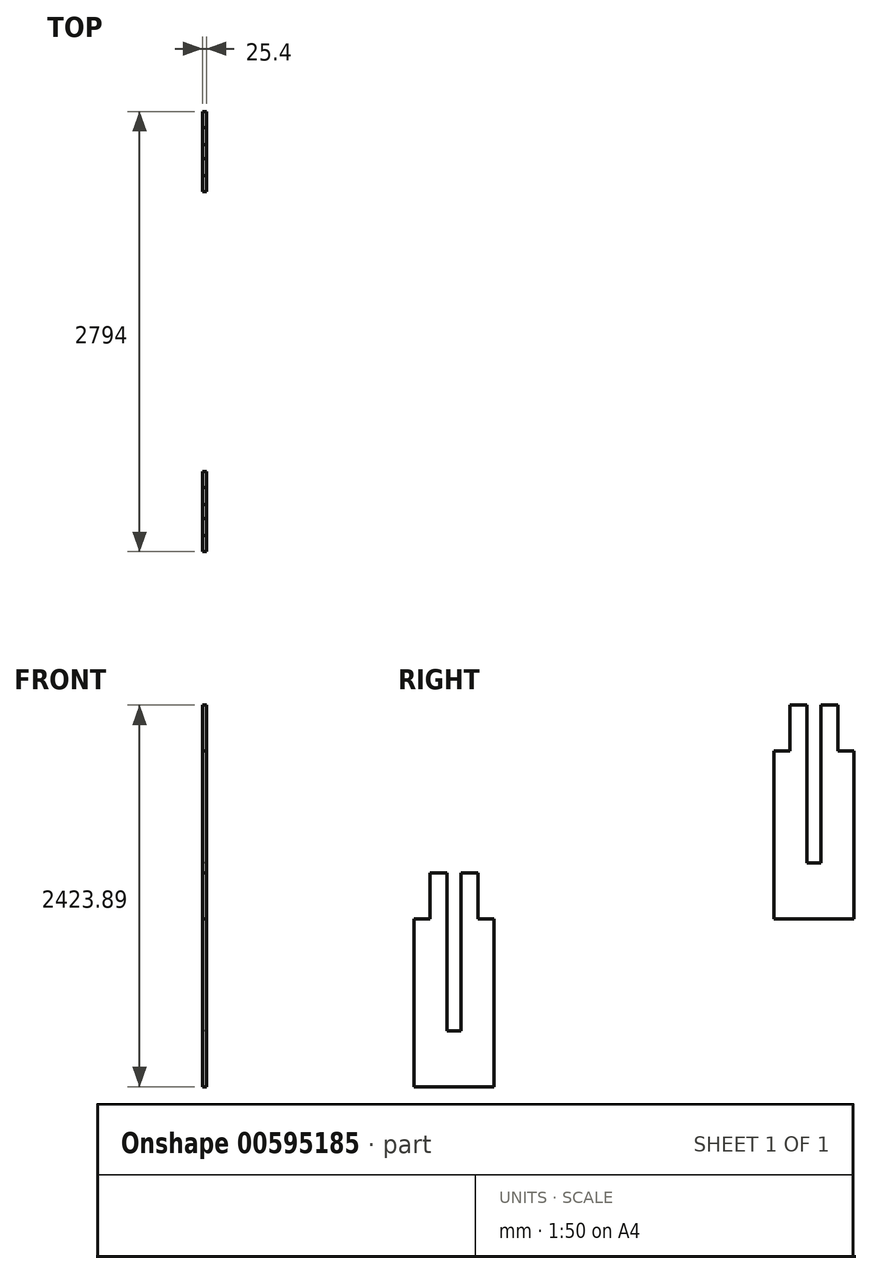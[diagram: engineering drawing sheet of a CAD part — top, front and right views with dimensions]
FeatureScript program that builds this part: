
annotation { "Feature Type Name" : "Feature", "Feature Type Description" : "" }
export const myFeature = defineFeature(function(context is Context, id is Id, definition is map)
    precondition{}
    {
        {
            var Q0;
            Q0=qCreatedBy(makeId("Right.planeOp"),FACE);
            var sketch = newSketch(context, id + "F0", { "sketchPlane" : qUnion([Q0])});
            skLineSegment(sketch, "E0.bottom", {"start": v(1143, -1143) * mm, "end": v(-1143, -1143) * mm});
            skLineSegment(sketch, "E0.right", {"start": v(-1143, -1143) * mm, "end": v(-1143, 1143) * mm});
            skPoint(sketch, "E0.middle", {"position": v(0, 0) * mm});
            skLineSegment(sketch, "E1", {"start": v(0, 0) * mm, "end": v(3173.99, 1480.05) * mm, "construction": true});
            skLineSegment(sketch, "E2", {"start": v(0, 0) * mm, "end": v(-5441.08, -2537.22) * mm, "construction": true});
            skPoint(sketch, "E3.middle", {"position": v(1143, 532.99) * mm});
            skLineSegment(sketch, "E4.bottom", {"start": v(889, 414.55) * mm, "end": v(990.6, 414.55) * mm});
            skLineSegment(sketch, "E4.top", {"start": v(889, -652.25) * mm, "end": v(1397, -652.25) * mm});
            skLineSegment(sketch, "E4.right", {"start": v(1397, 414.55) * mm, "end": v(1397, -652.25) * mm});
            skLineSegment(sketch, "E5", {"start": v(1295.4, 604.05) * mm, "end": v(1295.4, 705.65) * mm});
            skLineSegment(sketch, "E6", {"start": v(1295.4, 705.65) * mm, "end": v(1187.45, 705.65) * mm});
            skLineSegment(sketch, "E7", {"start": v(990.6, 705.65) * mm, "end": v(990.6, 414.55) * mm});
            skLineSegment(sketch, "E8", {"start": v(1295.4, 604.05) * mm, "end": v(1295.4, 414.55) * mm});
            skLineSegment(sketch, "E9", {"start": v(1187.45, 705.65) * mm, "end": v(1187.45, -296.65) * mm});
            skLineSegment(sketch, "E10", {"start": v(1187.45, -296.65) * mm, "end": v(1098.55, -296.65) * mm});
            skLineSegment(sketch, "E11", {"start": v(1098.55, -296.65) * mm, "end": v(1098.55, 705.65) * mm});
            skLineSegment(sketch, "E12.trimOffspring", {"start": v(1098.55, 705.65) * mm, "end": v(990.6, 705.65) * mm});
            skLineSegment(sketch, "E13.trimOffspring", {"start": v(1295.4, 414.55) * mm, "end": v(1397, 414.55) * mm});
            skLineSegment(sketch, "E14.trimOffspring", {"start": v(1143, 1066.39) * mm, "end": v(1143, 1143) * mm});
            skPoint(sketch, "E15.start.orphan", {"position": v(1143, 1066.39) * mm});
            skPoint(sketch, "E16.orphan", {"position": v(1098.55, 1066.39) * mm});
            skPoint(sketch, "E17.end.orphan", {"position": v(1187.45, 1066.39) * mm});
            skLineSegment(sketch, "E18", {"start": v(0, 0) * mm, "end": v(0, 464) * mm, "construction": true});
            skLineSegment(sketch, "E19", {"start": v(889, 414.55) * mm, "end": v(889, -652.25) * mm});
            skLineSegment(sketch, "E20", {"start": v(1143, 532.99) * mm, "end": v(4504.76, 532.99) * mm, "construction": true});
            skLineSegment(sketch, "E21", {"start": v(3173.99, 1480.05) * mm, "end": v(4504.76, 2100.6) * mm, "construction": true});
            skLineSegment(sketch, "E22", {"start": v(-1143, -532.99) * mm, "end": v(-4207, -532.99) * mm, "construction": true});
            skLineSegment(sketch, "E23", {"start": v(-4207, -532.99) * mm, "end": v(-4207, -1440.6) * mm, "construction": true});
            skLineSegment(sketch, "E24", {"start": v(4504.76, 2100.6) * mm, "end": v(6234.34, 2100.6) * mm, "construction": true});
            skLineSegment(sketch, "E25", {"start": v(-4207, -1440.6) * mm, "end": v(-5509.02, -1587.44) * mm, "construction": true});
            skSolve(sketch);
        }
        {
            var Q0;
            Q0 = qSketchRegion(id + "F0", true);
            extrude(context, id + "F1", {"entities" : qUnion([Q0]), "depth" : 25.4 * mm, "offsetDistance" : 25.4 * mm});
        }
        {
            var Q0;
            Q0=makeQuery(id+"F1.opExtrude","SWEPT_BODY",BODY,{"disambiguationData":[OSD([sQuery(id+"F0.wireOp",EDGE,"E4.bottom"),sQuery(id+"F0.wireOp",EDGE,"E4.top"),sQuery(id+"F0.wireOp",EDGE,"E4.right"),sQuery(id+"F0.wireOp",EDGE,"E5"),sQuery(id+"F0.wireOp",EDGE,"E6"),sQuery(id+"F0.wireOp",EDGE,"E7"),sQuery(id+"F0.wireOp",EDGE,"E8"),sQuery(id+"F0.wireOp",EDGE,"E9"),sQuery(id+"F0.wireOp",EDGE,"E10"),sQuery(id+"F0.wireOp",EDGE,"E11"),sQuery(id+"F0.wireOp",EDGE,"E12.trimOffspring"),sQuery(id+"F0.wireOp",EDGE,"E13.trimOffspring"),sQuery(id+"F0.wireOp",EDGE,"E19")])]});
            transform(context, id + "F2", {"entities" : qUnion([Q0]), "transformType" : TransformType.TRANSLATION_3D, "dx" : 0 * mm, "dy" : -2286 * mm, "dz" : -1066 * mm, "makeCopy" : true});
        }
    });
